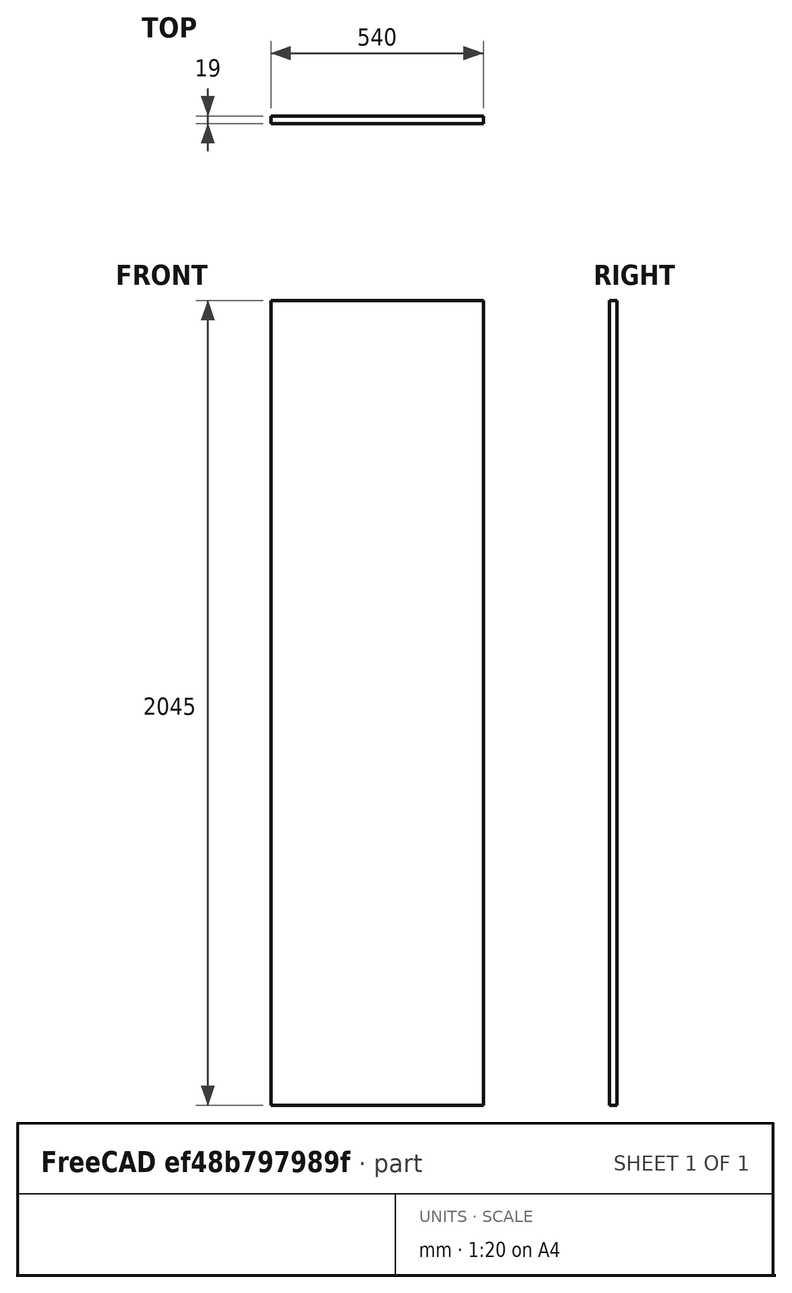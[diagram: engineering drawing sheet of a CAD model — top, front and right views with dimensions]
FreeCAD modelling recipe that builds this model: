
FCSTD DOCUMENT  (FreeCAD 1.0RUnknown)
Label: wardrobe_backplate_corpus00_jan
License: All rights reserved
LicenseURL: https://en.wikipedia.org/wiki/All_rights_reserved
objects: PartDesign::CoordinateSystem×2, Sketcher::SketchObject×1, PartDesign::Pad×1, PartDesign::Body×1
note: 8 computed .brp shape members not serialized (recipe doc carries the construction recipe); baked Part::Feature solids carry a one-line shape summary decoded from their .brp
EXTERNAL_REF file=../../mastersketch.FCStd obj=Spreadsheet

FEATURE [Sketcher::SketchObject] Sketch004
  ArcFitTolerance = 1e-06
  AttachmentSupport = -> [XZ_Plane006]
  FullyConstrained = true
  MakeInternals = false
  MapMode = 5
  Placement = pos=(0,0,0) rot=(1,0,0;1.5708rad)
  expr: Constraints[10] = mastersketch#Spreadsheet.corpus_width
  expr: Constraints[11] = mastersketch#Spreadsheet.corpus_height
  sketch-geometry (5):
    g0: LineSegment StartX=-270 StartY=-1022.5 StartZ=0 EndX=270 EndY=-1022.5 EndZ=0
    g1: LineSegment StartX=270 StartY=-1022.5 StartZ=0 EndX=270 EndY=1022.5 EndZ=0
    g2: LineSegment StartX=270 StartY=1022.5 StartZ=0 EndX=-270 EndY=1022.5 EndZ=0
    g3: LineSegment StartX=-270 StartY=1022.5 StartZ=0 EndX=-270 EndY=-1022.5 EndZ=0
    g4: GeomPoint [constr] X=0 Y=0 Z=0
  constraints (12):
    c: Coincident(g0,g1)
    c: Coincident(g1,g2)
    c: Coincident(g2,g3)
    c: Coincident(g3,g0)
    c: Horizontal(g0)
    c: Horizontal(g2)
    c: Vertical(g1)
    c: Vertical(g3)
    c: Symmetric(g2,g0,g4)
    c: Coincident(g4,g-1)
    c: DistanceX(g0,g0) = 540
    c: DistanceY(g3,g3) = 2045
FEATURE [PartDesign::Pad] Pad004
  Direction = (0,-1,2e-16)
  Length = 19
  Length2 = 10
  Placement = pos=(0,0,0) rot=(1,0,0;1.5708rad)
  Profile = -> Sketch004
  ReferenceAxis = -> Sketch004 [N_Axis]
  Refine = true
  Suppressed = false
  Type = 0
  expr: Length = mastersketch#Spreadsheet.corpus_backplate_thickness
FEATURE [PartDesign::CoordinateSystem] LCS_bottom
  AttacherType = Attacher::AttachEngine3D
  AttachmentSupport = -> [Pad004]
  MapMode = 45
  Placement = pos=(0,-19,-1022.5) rot=(0.57735,0.57735,0.57735;2.0944rad)
FEATURE [PartDesign::CoordinateSystem] LCS_back_right
  AttacherType = Attacher::AttachEngine3D
FEATURE [PartDesign::Body] Body004  label="wardrobe_backplate_corpus00_jan"
  AllowCompound = false
  Group = -> [Sketch004,Pad004,LCS_bottom,LCS_back_right]
  Origin = -> Origin006
  Tip = -> Pad004
